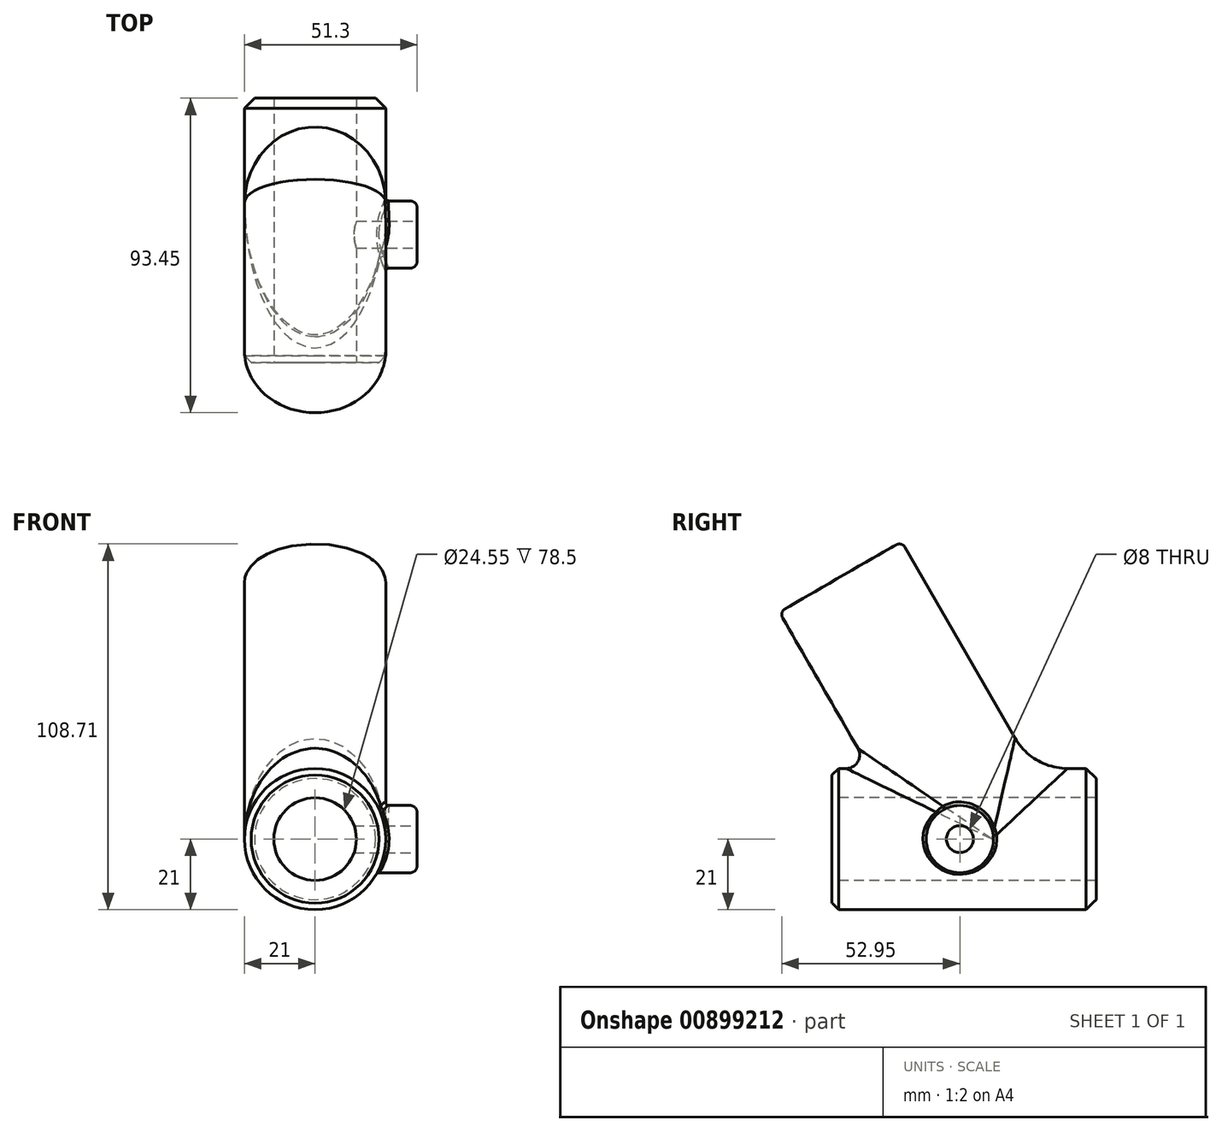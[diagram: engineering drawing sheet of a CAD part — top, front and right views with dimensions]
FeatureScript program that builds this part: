
annotation { "Feature Type Name" : "Feature", "Feature Type Description" : "" }
export const myFeature = defineFeature(function(context is Context, id is Id, definition is map)
    precondition{}
    {
        {
            var Q0;
            Q0=qCreatedBy(makeId("Front.planeOp"),FACE);
            var sketch = newSketch(context, id + "F0", { "sketchPlane" : qUnion([Q0])});
            skCircle(sketch, "E0", {"center": v(0, 0) * mm, "radius": 21 * mm});
            skSolve(sketch);
        }
        {
            var Q0;
            Q0=qSketchRegion(id+"F0",true);
            extrude(context, id + "F1", {"entities" : qUnion([Q0]), "oppositeDirection" : true, "depth" : 78.5 * mm, "offsetDistance" : 25 * mm});
        }
        {
            var Q0;
            Q0=qCreatedBy(makeId("Right.planeOp"),FACE);
            var sketch = newSketch(context, id + "F2", { "sketchPlane" : qUnion([Q0])});
            skLineSegment(sketch, "E1.0", {"start": v(29.31, -10.5) * mm, "end": v(-15.69, 67.44) * mm});
            skLineSegment(sketch, "E2", {"start": v(2.5, 77.94) * mm, "end": v(-15.69, 67.44) * mm});
            skLineSegment(sketch, "E3", {"start": v(47.5, 0) * mm, "end": v(29.31, -10.5) * mm});
            skLineSegment(sketch, "E4", {"start": v(2.5, 77.94) * mm, "end": v(47.5, 0) * mm});
            skSolve(sketch);
        }
        {
            var Q0;
            Q0=makeQuery(id+"F2.imprint","IMPRINT",FACE,{"disambiguationData":[TD([[makeQuery(id+"F2.imprint","IMPRINT",EDGE,{"derivedFrom":sQuery(id+"F2.wireOp",EDGE,"E1.0")}),-1.0]])]});
            var Q1;
            Q1=sQuery(id+"F2.wireOp",EDGE,"E4");
            revolve(context, id + "F3", {"operationType" : NewBodyOperationType.ADD, "surfaceOperationType" : NewSurfaceOperationType.NEW, "entities" : qUnion([Q0]), "axis" : qUnion([Q1]), "revolveType" : RevolveType.FULL});
        }
        {
            var Q0;
            Q0=makeQuery(id+"F3.boolean.opBoolean","INTERSECT",EDGE,{"disambiguationData":[OD(1.0)],"derivedFrom":[makeQuery(id+"F1.opExtrude","SWEPT_FACE",FACE,{"disambiguationData":[OSD([sQuery(id+"F0.wireOp",EDGE,"E0")])]}),makeQuery(id+"F3.opRevolve","SWEPT_FACE",FACE,{"disambiguationData":[OSD([sQuery(id+"F2.wireOp",EDGE,"E1.0")])]})]});
            fillet(context, id + "F4", {"entities" : qUnion([Q0]), "radius" : 18 * mm, "tangentPropagation" : true, "allowEdgeOverflow" : false});
        }
        {
            var Q0;
            Q0=makeQuery(id+"F3.boolean.opBoolean","INTERSECT",EDGE,{"disambiguationData":[OD(0.0)],"derivedFrom":[makeQuery(id+"F1.opExtrude","SWEPT_FACE",FACE,{"disambiguationData":[OSD([sQuery(id+"F0.wireOp",EDGE,"E0")])]}),makeQuery(id+"F3.opRevolve","SWEPT_FACE",FACE,{"disambiguationData":[OSD([sQuery(id+"F2.wireOp",EDGE,"E1.0")])]})]});
            fillet(context, id + "F5", {"entities" : qUnion([Q0]), "radius" : 4 * mm, "tangentPropagation" : true, "allowEdgeOverflow" : false});
        }
        {
            var Q0;
            Q0=makeQuery(id+"F1.opExtrude","CAP_FACE",FACE,{"disambiguationData":[OSD([sQuery(id+"F0.wireOp",EDGE,"E0")])],"isStart":true});
            var sketch = newSketch(context, id + "F6", { "sketchPlane" : qUnion([Q0])});
            skCircle(sketch, "E5", {"center": v(0, 0) * mm, "radius": 12.28 * mm});
            skSolve(sketch);
        }
        {
            var Q0;
            Q0=qSketchRegion(id+"F6",true);
            extrude(context, id + "F7", {"entities" : qUnion([Q0]), "operationType" : NewBodyOperationType.REMOVE, "oppositeDirection" : true, "depth" : 78.5 * mm, "offsetDistance" : 25 * mm});
        }
        {
            var Q0;
            Q0=makeQuery(id+"F1.opExtrude","CAP_EDGE",EDGE,{"disambiguationData":[OSD([sQuery(id+"F0.wireOp",EDGE,"E0")])],"isStart":false});
            chamfer(context, id + "F8", {"entities" : qUnion([Q0]), "width" : 3 * mm, "tangentPropagation" : true});
        }
        {
            var Q0;
            Q0=makeQuery(id+"F3.opRevolve","SWEPT_EDGE",EDGE,{"disambiguationData":[OSD([sQuery(id+"F2.wireOp",EDGE,"E1.0"),sQuery(id+"F2.wireOp",EDGE,"E2")])]});
            fillet(context, id + "F9", {"entities" : qUnion([Q0]), "radius" : 2 * mm, "tangentPropagation" : true, "allowEdgeOverflow" : false});
        }
        {
            var Q0;
            Q0=makeQuery(id+"F1.opExtrude","CAP_EDGE",EDGE,{"disambiguationData":[OSD([sQuery(id+"F0.wireOp",EDGE,"E0")])],"isStart":true});
            chamfer(context, id + "F10", {"entities" : qUnion([Q0]), "width" : 2 * mm, "tangentPropagation" : true});
        }
        {
            var Q0;
            Q0=qCreatedBy(makeId("Right.planeOp"),FACE);
            cPlane(context, id + "F11", {"entities" : qUnion([Q0]), "cplaneType" : CPlaneType.OFFSET, "offset" : 21 * mm, "width" : 150 * mm, "height" : 150 * mm});
        }
        {
            var Q0;
            Q0=qCreatedBy(id+"F11.planeOp",FACE);
            var sketch = newSketch(context, id + "F12", { "sketchPlane" : qUnion([Q0])});
            skCircle(sketch, "E6", {"center": v(38, 0) * mm, "radius": 10 * mm});
            skSolve(sketch);
        }
        {
            var Q0;
            Q0=qSketchRegion(id+"F12",true);
            extrude(context, id + "F13", {"entities" : qUnion([Q0]), "operationType" : NewBodyOperationType.ADD, "oppositeDirection" : true, "depth" : 3 * mm, "offsetDistance" : 25 * mm});
        }
        {
            var Q0;
            Q0=makeQuery(id+"F13.opExtrude","CAP_FACE",FACE,{"disambiguationData":[OSD([sQuery(id+"F12.wireOp",EDGE,"E6")])],"isStart":true});
            extrude(context, id + "F14", {"entities" : qUnion([Q0]), "operationType" : NewBodyOperationType.ADD, "depth" : 9.3 * mm, "offsetDistance" : 25 * mm});
        }
        {
            var Q0;
            Q0=makeQuery(id+"F14.opExtrude","CAP_EDGE",EDGE,{"disambiguationData":[OSD([sQuery(id+"F12.wireOp",EDGE,"E6")])],"isStart":false});
            fillet(context, id + "F15", {"entities" : qUnion([Q0]), "radius" : 2 * mm, "tangentPropagation" : true, "allowEdgeOverflow" : false});
        }
        {
            var Q0;
            Q0=makeQuery(id+"F14.opExtrude","CAP_FACE",FACE,{"disambiguationData":[OSD([sQuery(id+"F12.wireOp",EDGE,"E6")])],"isStart":false});
            var sketch = newSketch(context, id + "F16", { "sketchPlane" : qUnion([Q0])});
            skCircle(sketch, "E7", {"center": v(38, 0) * mm, "radius": 4 * mm});
            skSolve(sketch);
        }
        {
            var Q0;
            Q0=qSketchRegion(id+"F16",true);
            extrude(context, id + "F17", {"entities" : qUnion([Q0]), "operationType" : NewBodyOperationType.REMOVE, "oppositeDirection" : true, "depth" : 25 * mm, "offsetDistance" : 25 * mm});
        }
        {
            var Q0;
            {var subQ0=sQuery(id+"F12.wireOp",EDGE,"E6");var subQ1=makeQuery(id+"F13.opExtrude","SWEPT_FACE",FACE,{"disambiguationData":[OSD([subQ0])]});var subQ2=sQuery(id+"F2.wireOp",EDGE,"E1.0");var subQ3=sQuery(id+"F0.wireOp",EDGE,"E0");var subQ4=makeQuery(id+"F3.opRevolve","SWEPT_FACE",FACE,{"disambiguationData":[OSD([subQ2])]});var subQ5=makeQuery(id+"F1.opExtrude","SWEPT_FACE",FACE,{"disambiguationData":[OSD([subQ3])]});var subQ6=makeQuery(id+"F13.opExtrude","CAP_FACE",FACE,{"disambiguationData":[OSD([subQ0])],"isStart":true});Q0=makeQuery(id+"F14.boolean.opBoolean","MERGE",FACE,{"derivedFrom":[makeQuery(id+"F13.boolean.opBoolean","SPLIT",FACE,{"disambiguationData":[TD([subQ5,subQ1,subQ6])],"derivedFrom":subQ1}),makeQuery(id+"F13.boolean.opBoolean","SPLIT",FACE,{"disambiguationData":[TD([subQ5,subQ4,makeQuery(id+"F4.opFillet","BLEND_FACE",FACE,{"disambiguationData":[OSD([subQ3,subQ2])]}),subQ1,subQ6])],"derivedFrom":subQ1}),makeQuery(id+"F13.boolean.opBoolean","SPLIT",FACE,{"disambiguationData":[TD([subQ5,subQ4,makeQuery(id+"F5.opFillet","BLEND_FACE",FACE,{"disambiguationData":[OSD([subQ3,subQ2])]}),subQ1,subQ6])],"derivedFrom":subQ1}),makeQuery(id+"F14.opExtrude","SWEPT_FACE",FACE,{"disambiguationData":[OSD([subQ0])]})]});}
            var Q1;
            Q1=makeQuery(id+"F7.boolean.opBoolean","COPY",EDGE,{"derivedFrom":makeQuery(id+"F7.opExtrude","CAP_EDGE",EDGE,{"disambiguationData":[OSD([sQuery(id+"F6.wireOp",EDGE,"E5")])],"isStart":true})});
            var Q2;
            Q2=makeQuery(id+"F7.boolean.opBoolean","COPY",EDGE,{"derivedFrom":makeQuery(id+"F7.opExtrude","CAP_EDGE",EDGE,{"disambiguationData":[OSD([sQuery(id+"F6.wireOp",EDGE,"E5")])],"isStart":false})});
            var Q3;
            Q3=makeQuery(id+"F17.boolean.opBoolean","COPY",EDGE,{"derivedFrom":makeQuery(id+"F17.opExtrude","CAP_EDGE",EDGE,{"disambiguationData":[OSD([sQuery(id+"F16.wireOp",EDGE,"E7")])],"isStart":true})});
            fillet(context, id + "F18", {"entities" : qUnion([Q0, Q1, Q2, Q3]), "radius" : 1 * mm, "tangentPropagation" : true, "allowEdgeOverflow" : false});
        }
    });
